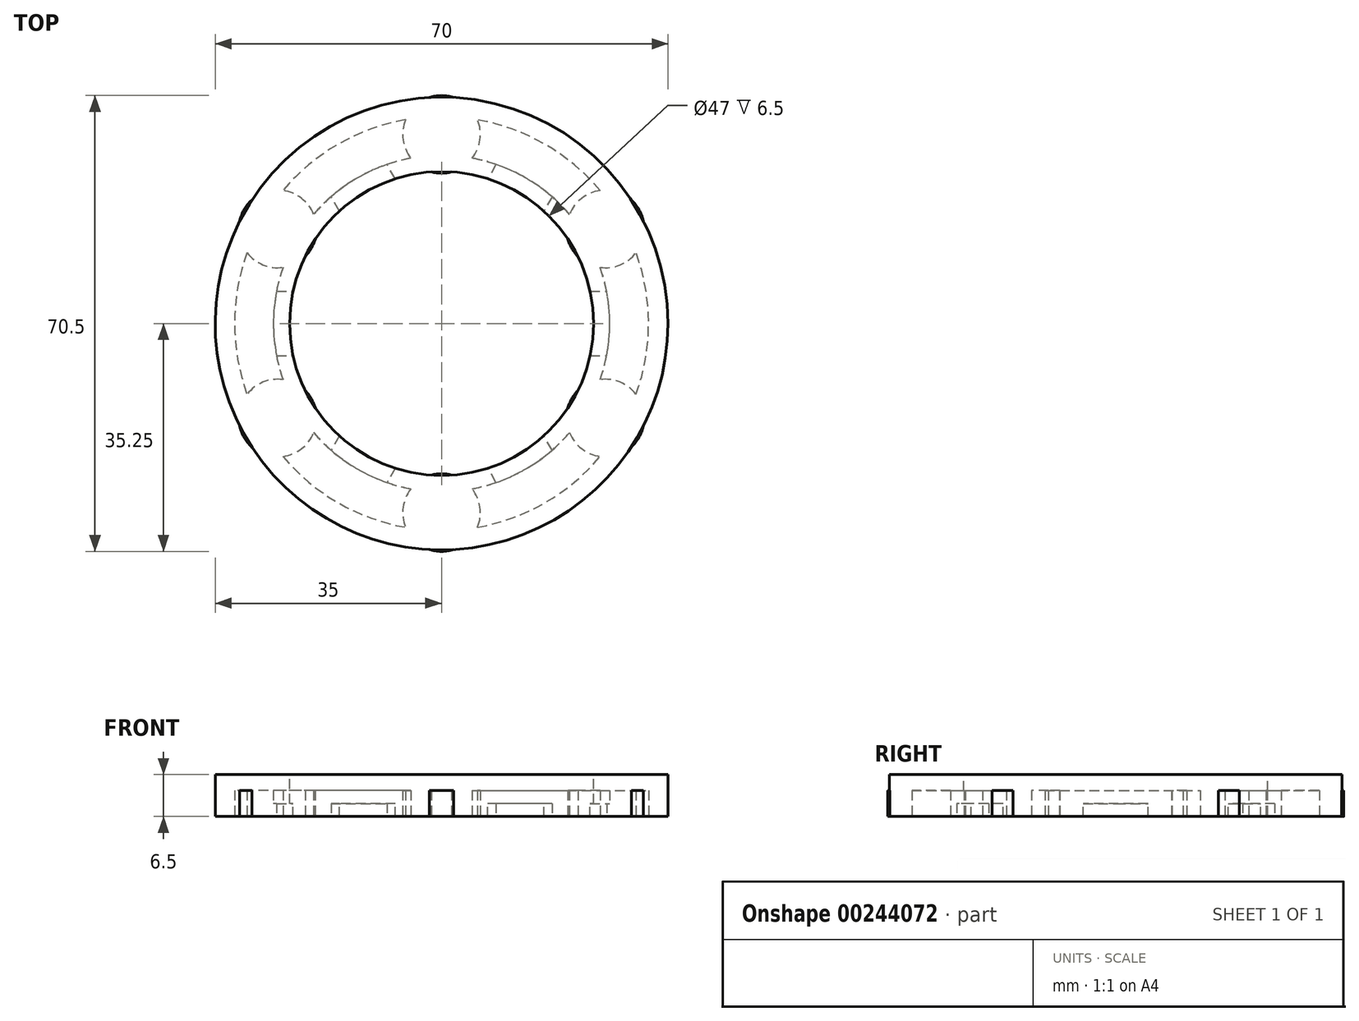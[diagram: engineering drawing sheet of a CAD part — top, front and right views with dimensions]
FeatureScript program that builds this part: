
annotation { "Feature Type Name" : "Feature", "Feature Type Description" : "" }
export const myFeature = defineFeature(function(context is Context, id is Id, definition is map)
    precondition{}
    {
        {
            var Q0;
            Q0=qCreatedBy(makeId("Top.planeOp"),FACE);
            var sketch = newSketch(context, id + "F0", { "sketchPlane" : qUnion([Q0])});
            skCircle(sketch, "E0", {"center": v(0, 0) * mm, "radius": 35 * mm});
            skSolve(sketch);
        }
        {
            var Q0;
            Q0=makeQuery(id+"F0.imprint","IMPRINT",FACE,{"disambiguationData":[TD([[makeQuery(id+"F0.imprint","IMPRINT",EDGE,{"derivedFrom":sQuery(id+"F0.wireOp",EDGE,"E0")}),1.0]])]});
            extrude(context, id + "F1", {"entities" : qUnion([Q0]), "depth" : 6.5 * mm});
        }
        {
            var Q0;
            Q0=makeQuery(id+"F1.opExtrude","CAP_FACE",FACE,{"disambiguationData":[OSD([sQuery(id+"F0.wireOp",EDGE,"E0")])],"isStart":false});
            var sketch = newSketch(context, id + "F2", { "sketchPlane" : qUnion([Q0])});
            skCircle(sketch, "E1", {"center": v(0, 0) * mm, "radius": 23.5 * mm});
            skSolve(sketch);
        }
        {
            var Q0;
            Q0=makeQuery(id+"F2.imprint","IMPRINT",FACE,{"disambiguationData":[TD([[makeQuery(id+"F2.imprint","IMPRINT",EDGE,{"derivedFrom":sQuery(id+"F2.wireOp",EDGE,"E1")}),1.0]])]});
            extrude(context, id + "F3", {"entities" : qUnion([Q0]), "operationType" : NewBodyOperationType.REMOVE, "endBound" : BoundingType.UP_TO_NEXT, "oppositeDirection" : true, "depth" : 25 * mm});
        }
        {
            var Q0;
            Q0=makeQuery(id+"F1.opExtrude","CAP_FACE",FACE,{"disambiguationData":[OSD([sQuery(id+"F0.wireOp",EDGE,"E0")])],"isStart":true});
            var sketch = newSketch(context, id + "F4", { "sketchPlane" : qUnion([Q0])});
            skCircle(sketch, "E2.0", {"center": v(0, 0) * mm, "radius": 32 * mm});
            skCircle(sketch, "E3.0", {"center": v(0, 0) * mm, "radius": 26 * mm});
            skSolve(sketch);
        }
        {
            var Q0;
            Q0=makeQuery(id+"F4.imprint","IMPRINT",FACE,{"disambiguationData":[TD([[makeQuery(id+"F4.imprint","IMPRINT",EDGE,{"derivedFrom":sQuery(id+"F4.wireOp",EDGE,"E2.0")}),1.0]])]});
            extrude(context, id + "F5", {"entities" : qUnion([Q0]), "operationType" : NewBodyOperationType.REMOVE, "oppositeDirection" : true, "depth" : 4 * mm});
        }
        {
            var Q0;
            Q0=qCreatedBy(makeId("Top.planeOp"),FACE);
            var sketch = newSketch(context, id + "F6", { "sketchPlane" : qUnion([Q0])});
            skLineSegment(sketch, "E4.bottom", {"start": v(-26, -5) * mm, "end": v(-8.66, -5) * mm});
            skLineSegment(sketch, "E4.top", {"start": v(-26, 5) * mm, "end": v(-8.66, 5) * mm});
            skLineSegment(sketch, "E4.left", {"start": v(-26, -5) * mm, "end": v(-26, 5) * mm});
            skLineSegment(sketch, "E4.right", {"start": v(26, -5) * mm, "end": v(26, 5) * mm});
            skLineSegment(sketch, "E5.1.0", {"start": v(17.33, -20.02) * mm, "end": v(8.67, -25.02) * mm});
            skLineSegment(sketch, "E5.1.1", {"start": v(17.33, -20.02) * mm, "end": v(8.66, -5) * mm});
            skLineSegment(sketch, "E5.1.2", {"start": v(-8.67, 25.02) * mm, "end": v(-17.33, 20.02) * mm});
            skLineSegment(sketch, "E5.1.3", {"start": v(8.67, -25.02) * mm, "end": v(0, -10) * mm});
            skLineSegment(sketch, "E5.2.0", {"start": v(8.67, 25.02) * mm, "end": v(17.33, 20.02) * mm});
            skLineSegment(sketch, "E5.2.1", {"start": v(8.67, 25.02) * mm, "end": v(0, 10) * mm});
            skLineSegment(sketch, "E5.2.2", {"start": v(-17.33, -20.02) * mm, "end": v(-8.67, -25.02) * mm});
            skLineSegment(sketch, "E5.2.3", {"start": v(17.33, 20.02) * mm, "end": v(8.66, 5) * mm});
            skPoint(sketch, "E5.center", {"position": v(0, 0) * mm});
            skLineSegment(sketch, "E6.trimOffspring", {"start": v(-8.66, 5) * mm, "end": v(-17.33, 20.02) * mm});
            skLineSegment(sketch, "E7.trimOffspring", {"start": v(8.66, -5) * mm, "end": v(26, -5) * mm});
            skLineSegment(sketch, "E8.trimOffspring", {"start": v(0, -10) * mm, "end": v(-8.67, -25.02) * mm});
            skLineSegment(sketch, "E9.trimOffspring", {"start": v(0, 10) * mm, "end": v(-8.67, 25.02) * mm});
            skLineSegment(sketch, "E10.trimOffspring", {"start": v(-8.66, -5) * mm, "end": v(-17.33, -20.02) * mm});
            skLineSegment(sketch, "E11.trimOffspring", {"start": v(8.66, 5) * mm, "end": v(26, 5) * mm});
            skSolve(sketch);
        }
        {
            var Q0;
            Q0=makeQuery(id+"F6.imprint","IMPRINT",FACE,{"disambiguationData":[TD([[makeQuery(id+"F6.imprint","IMPRINT",EDGE,{"derivedFrom":sQuery(id+"F6.wireOp",EDGE,"E4.bottom")}),1.0]])]});
            extrude(context, id + "F7", {"entities" : qUnion([Q0]), "operationType" : NewBodyOperationType.REMOVE, "depth" : 2 * mm});
        }
        {
            var Q0;
            Q0=qCreatedBy(makeId("Top.planeOp"),FACE);
            var sketch = newSketch(context, id + "F8", { "sketchPlane" : qUnion([Q0])});
            skCircle(sketch, "E12", {"center": v(0, -29.25) * mm, "radius": 6 * mm});
            skCircle(sketch, "E13.1.0", {"center": v(25.33, -14.63) * mm, "radius": 6 * mm});
            skCircle(sketch, "E13.2.0", {"center": v(25.33, 14.62) * mm, "radius": 6 * mm});
            skCircle(sketch, "E13.3.0", {"center": v(0, 29.25) * mm, "radius": 6 * mm});
            skCircle(sketch, "E13.4.0", {"center": v(-25.33, 14.63) * mm, "radius": 6 * mm});
            skCircle(sketch, "E13.5.0", {"center": v(-25.33, -14.63) * mm, "radius": 6 * mm});
            skPoint(sketch, "E13.center", {"position": v(0, 0) * mm});
            skSolve(sketch);
        }
        {
            var Q0;
            Q0 = qSketchRegion(id + "F8", true);
            extrude(context, id + "F9", {"entities" : qUnion([Q0]), "operationType" : NewBodyOperationType.ADD, "depth" : 4 * mm});
        }
    });
